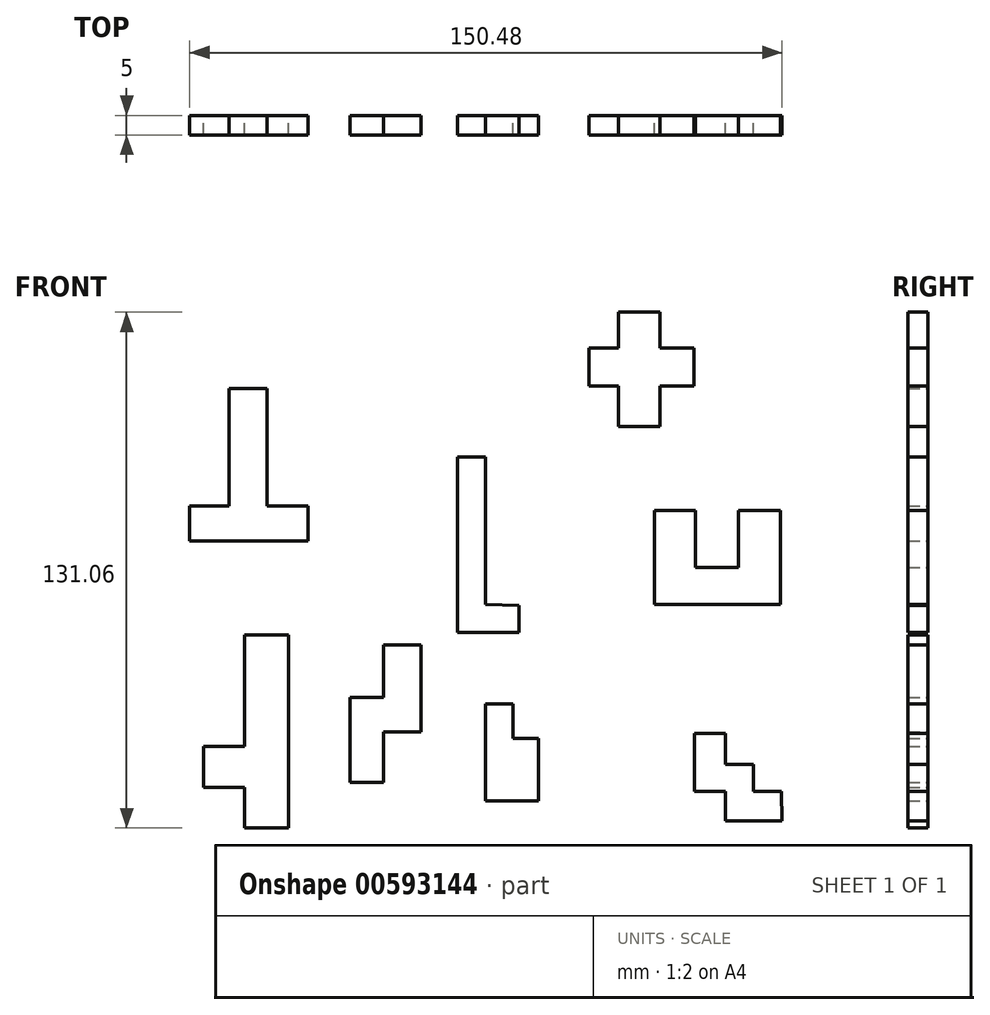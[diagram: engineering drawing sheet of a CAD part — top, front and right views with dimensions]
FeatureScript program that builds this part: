
annotation { "Feature Type Name" : "Feature", "Feature Type Description" : "" }
export const myFeature = defineFeature(function(context is Context, id is Id, definition is map)
    precondition{}
    {
        {
            var Q0;
            Q0=qCreatedBy(makeId("Front.planeOp"),FACE);
            var sketch = newSketch(context, id + "F0", { "sketchPlane" : qUnion([Q0])});
            skLineSegment(sketch, "E0", {"start": v(0, 37.46) * mm, "end": v(0, 0) * mm});
            skLineSegment(sketch, "E1", {"start": v(0, 37.46) * mm, "end": v(-7.2, 37.46) * mm});
            skLineSegment(sketch, "E2", {"start": v(-7.2, 37.46) * mm, "end": v(-7.2, -7.02) * mm});
            skLineSegment(sketch, "E3", {"start": v(-7.2, -7.02) * mm, "end": v(8.48, -7.02) * mm});
            skLineSegment(sketch, "E4", {"start": v(8.48, -7.02) * mm, "end": v(8.48, 0) * mm});
            skLineSegment(sketch, "E5", {"start": v(8.66, -0.27) * mm, "end": v(0, 0) * mm});
            skSolve(sketch);
        }
        {
            var Q0;
            Q0 = qSketchRegion(id + "F0", true);
            extrude(context, id + "F1", {"entities" : qUnion([Q0]), "depth" : 5 * mm, "offsetDistance" : 25 * mm});
        }
        {
            var Q0;
            Q0=qCreatedBy(makeId("Front.planeOp"),FACE);
            var sketch = newSketch(context, id + "F2", { "sketchPlane" : qUnion([Q0])});
            skLineSegment(sketch, "E6", {"start": v(-65.17, 54.96) * mm, "end": v(-65.17, 25.07) * mm});
            skLineSegment(sketch, "E7", {"start": v(-65.17, 25.07) * mm, "end": v(-75.2, 25.07) * mm});
            skLineSegment(sketch, "E8", {"start": v(-75.2, 25.07) * mm, "end": v(-75.2, 16.13) * mm});
            skLineSegment(sketch, "E9", {"start": v(-75.2, 16.13) * mm, "end": v(-45.12, 16.13) * mm});
            skLineSegment(sketch, "E10", {"start": v(-45.12, 16.13) * mm, "end": v(-45.12, 25.07) * mm});
            skLineSegment(sketch, "E11", {"start": v(-45.12, 25.07) * mm, "end": v(-55.5, 25.07) * mm});
            skLineSegment(sketch, "E12", {"start": v(-55.5, 25.07) * mm, "end": v(-55.5, 54.96) * mm});
            skLineSegment(sketch, "E13", {"start": v(-55.5, 54.96) * mm, "end": v(-65.17, 54.96) * mm});
            skSolve(sketch);
        }
        {
            var Q0;
            Q0 = qSketchRegion(id + "F2", true);
            extrude(context, id + "F3", {"entities" : qUnion([Q0]), "depth" : 5 * mm, "offsetDistance" : 25 * mm});
        }
        {
            var Q0;
            Q0=qCreatedBy(makeId("Front.planeOp"),FACE);
            var sketch = newSketch(context, id + "F4", { "sketchPlane" : qUnion([Q0])});
            skLineSegment(sketch, "E14", {"start": v(74.92, 23.97) * mm, "end": v(74.92, 0) * mm});
            skLineSegment(sketch, "E15", {"start": v(74.92, 0) * mm, "end": v(42.83, 0) * mm});
            skLineSegment(sketch, "E16", {"start": v(42.83, 0) * mm, "end": v(42.83, 23.97) * mm});
            skLineSegment(sketch, "E17", {"start": v(42.83, 23.97) * mm, "end": v(53.22, 23.97) * mm});
            skLineSegment(sketch, "E18", {"start": v(53.22, 23.97) * mm, "end": v(53.22, 9.39) * mm});
            skLineSegment(sketch, "E19", {"start": v(53.22, 9.39) * mm, "end": v(64.16, 9.39) * mm});
            skLineSegment(sketch, "E20", {"start": v(64.16, 9.39) * mm, "end": v(64.16, 23.97) * mm});
            skLineSegment(sketch, "E21", {"start": v(64.16, 23.97) * mm, "end": v(74.92, 23.97) * mm});
            skSolve(sketch);
        }
        {
            var Q0;
            Q0 = qSketchRegion(id + "F4", true);
            extrude(context, id + "F5", {"entities" : qUnion([Q0]), "depth" : 5 * mm, "offsetDistance" : 25 * mm});
        }
        {
            var Q0;
            Q0=qCreatedBy(makeId("Front.planeOp"),FACE);
            var sketch = newSketch(context, id + "F6", { "sketchPlane" : qUnion([Q0])});
            skLineSegment(sketch, "E22", {"start": v(-61.26, -56.78) * mm, "end": v(-50.14, -56.78) * mm});
            skLineSegment(sketch, "E23", {"start": v(-50.14, -56.78) * mm, "end": v(-50.14, -46.4) * mm});
            skLineSegment(sketch, "E24", {"start": v(-61.26, -56.78) * mm, "end": v(-61.26, -46.4) * mm});
            skLineSegment(sketch, "E25", {"start": v(-61.26, -46.4) * mm, "end": v(-71.65, -46.4) * mm});
            skLineSegment(sketch, "E26", {"start": v(-71.65, -46.4) * mm, "end": v(-71.65, -36) * mm});
            skLineSegment(sketch, "E27", {"start": v(-71.65, -36) * mm, "end": v(-61.26, -36) * mm});
            skLineSegment(sketch, "E28", {"start": v(-61.26, -36) * mm, "end": v(-61.26, -7.75) * mm});
            skLineSegment(sketch, "E29", {"start": v(-61.26, -7.75) * mm, "end": v(-50.14, -7.75) * mm});
            skLineSegment(sketch, "E30", {"start": v(-50.14, -7.75) * mm, "end": v(-50.14, -46.4) * mm});
            skSolve(sketch);
        }
        {
            var Q0;
            Q0 = qSketchRegion(id + "F6", true);
            extrude(context, id + "F7", {"entities" : qUnion([Q0]), "depth" : 5 * mm, "offsetDistance" : 25 * mm});
        }
        {
            var Q0;
            Q0=qCreatedBy(makeId("Front.planeOp"),FACE);
            var sketch = newSketch(context, id + "F8", { "sketchPlane" : qUnion([Q0])});
            skLineSegment(sketch, "E31", {"start": v(33.72, 74.28) * mm, "end": v(44.3, 74.28) * mm});
            skLineSegment(sketch, "E32", {"start": v(44.3, 74.28) * mm, "end": v(44.3, 65.17) * mm});
            skLineSegment(sketch, "E33", {"start": v(44.3, 65.17) * mm, "end": v(52.86, 65.17) * mm});
            skLineSegment(sketch, "E34", {"start": v(52.86, 65.17) * mm, "end": v(52.86, 55.5) * mm});
            skLineSegment(sketch, "E35", {"start": v(52.86, 55.5) * mm, "end": v(44.3, 55.5) * mm});
            skLineSegment(sketch, "E36", {"start": v(44.3, 55.5) * mm, "end": v(44.3, 45.3) * mm});
            skLineSegment(sketch, "E37", {"start": v(44.3, 45.3) * mm, "end": v(33.72, 45.3) * mm});
            skLineSegment(sketch, "E38", {"start": v(33.72, 45.3) * mm, "end": v(33.72, 55.5) * mm});
            skLineSegment(sketch, "E39", {"start": v(26.24, 65.17) * mm, "end": v(33.72, 65.17) * mm});
            skLineSegment(sketch, "E40", {"start": v(33.72, 65.17) * mm, "end": v(33.72, 74.28) * mm});
            skLineSegment(sketch, "E41", {"start": v(26.24, 65.17) * mm, "end": v(26.24, 55.5) * mm});
            skLineSegment(sketch, "E42", {"start": v(26.24, 55.5) * mm, "end": v(33.72, 55.5) * mm});
            skSolve(sketch);
        }
        {
            var Q0;
            Q0 = qSketchRegion(id + "F8", true);
            extrude(context, id + "F9", {"entities" : qUnion([Q0]), "depth" : 5 * mm, "offsetDistance" : 25 * mm});
        }
        {
            var Q0;
            Q0=qCreatedBy(makeId("Front.planeOp"),FACE);
            var sketch = newSketch(context, id + "F10", { "sketchPlane" : qUnion([Q0])});
            skLineSegment(sketch, "E43", {"start": v(75.28, -54.96) * mm, "end": v(60.88, -54.96) * mm});
            skLineSegment(sketch, "E44", {"start": v(60.88, -54.96) * mm, "end": v(60.88, -47.49) * mm});
            skLineSegment(sketch, "E45", {"start": v(60.88, -47.49) * mm, "end": v(53.04, -47.49) * mm});
            skLineSegment(sketch, "E46", {"start": v(53.04, -47.49) * mm, "end": v(53.04, -32.72) * mm});
            skLineSegment(sketch, "E47", {"start": v(53.04, -32.72) * mm, "end": v(60.88, -32.72) * mm});
            skLineSegment(sketch, "E48", {"start": v(60.88, -32.72) * mm, "end": v(60.88, -40.56) * mm});
            skLineSegment(sketch, "E49", {"start": v(60.88, -40.56) * mm, "end": v(67.99, -40.56) * mm});
            skLineSegment(sketch, "E50", {"start": v(67.99, -40.56) * mm, "end": v(67.99, -47.49) * mm});
            skLineSegment(sketch, "E51", {"start": v(67.99, -47.49) * mm, "end": v(75.1, -47.49) * mm});
            skLineSegment(sketch, "E52", {"start": v(75.1, -47.49) * mm, "end": v(75.28, -54.96) * mm});
            skSolve(sketch);
        }
        {
            var Q0;
            Q0 = qSketchRegion(id + "F10", true);
            extrude(context, id + "F11", {"entities" : qUnion([Q0]), "depth" : 5 * mm, "offsetDistance" : 25 * mm});
        }
        {
            var Q0;
            Q0=qCreatedBy(makeId("Front.planeOp"),FACE);
            var sketch = newSketch(context, id + "F12", { "sketchPlane" : qUnion([Q0])});
            skLineSegment(sketch, "E53", {"start": v(0, -34) * mm, "end": v(0, -49.86) * mm});
            skLineSegment(sketch, "E54", {"start": v(0, -49.86) * mm, "end": v(13.44, -49.86) * mm});
            skLineSegment(sketch, "E55", {"start": v(13.44, -49.86) * mm, "end": v(13.44, -34) * mm});
            skLineSegment(sketch, "E56", {"start": v(0, -34) * mm, "end": v(0, -25.25) * mm});
            skLineSegment(sketch, "E57", {"start": v(0, -25.25) * mm, "end": v(6.88, -25.25) * mm});
            skLineSegment(sketch, "E58", {"start": v(6.88, -25.25) * mm, "end": v(6.88, -34) * mm});
            skLineSegment(sketch, "E59", {"start": v(6.88, -34) * mm, "end": v(13.44, -34) * mm});
            skSolve(sketch);
        }
        {
            var Q0;
            Q0 = qSketchRegion(id + "F12", true);
            extrude(context, id + "F13", {"entities" : qUnion([Q0]), "depth" : 5 * mm, "offsetDistance" : 25 * mm});
        }
        {
            var Q0;
            Q0=qCreatedBy(makeId("Front.planeOp"),FACE);
            var sketch = newSketch(context, id + "F14", { "sketchPlane" : qUnion([Q0])});
            skLineSegment(sketch, "E60", {"start": v(-25.93, -10.3) * mm, "end": v(-16.45, -10.3) * mm});
            skLineSegment(sketch, "E61", {"start": v(-16.45, -10.3) * mm, "end": v(-16.45, -32.36) * mm});
            skLineSegment(sketch, "E62", {"start": v(-25.93, -10.3) * mm, "end": v(-25.93, -23.6) * mm});
            skLineSegment(sketch, "E63", {"start": v(-25.93, -23.6) * mm, "end": v(-34.5, -23.6) * mm});
            skLineSegment(sketch, "E64", {"start": v(-34.5, -23.6) * mm, "end": v(-34.5, -45.12) * mm});
            skLineSegment(sketch, "E65", {"start": v(-34.5, -45.12) * mm, "end": v(-25.93, -45.12) * mm});
            skLineSegment(sketch, "E66", {"start": v(-25.93, -45.12) * mm, "end": v(-25.93, -32.36) * mm});
            skLineSegment(sketch, "E67", {"start": v(-25.93, -32.36) * mm, "end": v(-16.45, -32.36) * mm});
            skSolve(sketch);
        }
        {
            var Q0;
            Q0 = qSketchRegion(id + "F14", true);
            extrude(context, id + "F15", {"entities" : qUnion([Q0]), "depth" : 5 * mm, "offsetDistance" : 25 * mm});
        }
    });
